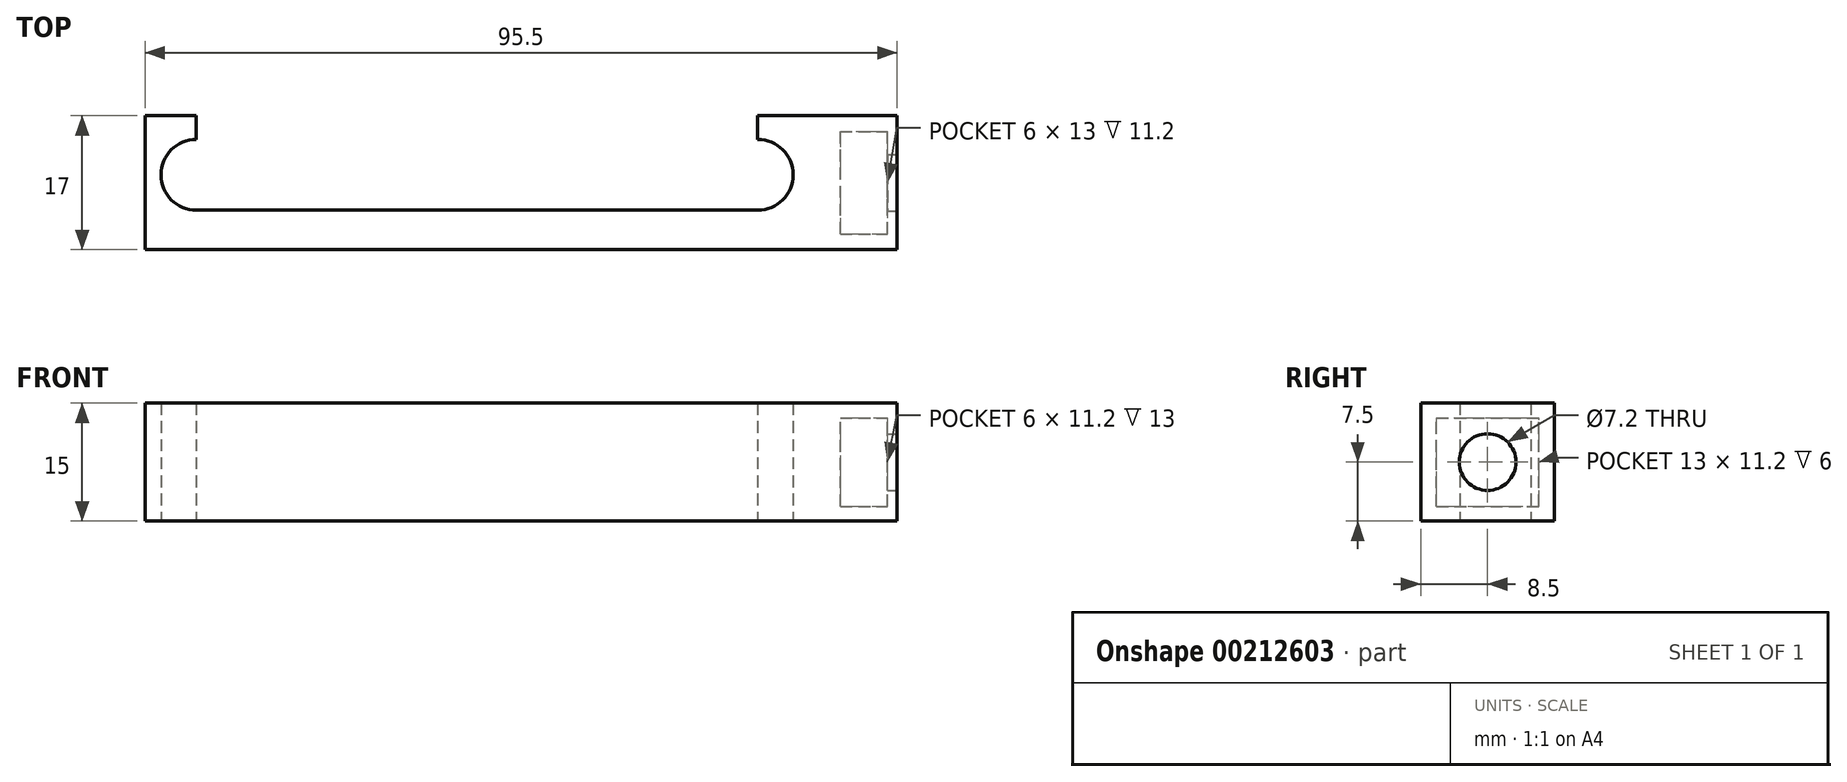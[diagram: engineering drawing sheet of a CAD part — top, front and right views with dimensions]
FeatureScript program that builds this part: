
annotation { "Feature Type Name" : "Feature", "Feature Type Description" : "" }
export const myFeature = defineFeature(function(context is Context, id is Id, definition is map)
    precondition{}
    {
        {
            var Q0;
            Q0=qCreatedBy(makeId("Top.planeOp"),FACE);
            var sketch = newSketch(context, id + "F0", { "sketchPlane" : qUnion([Q0])});
            skLineSegment(sketch, "E0.bottom", {"start": v(35.65, -4.5) * mm, "end": v(-35.65, -4.5) * mm});
            skLineSegment(sketch, "E0.left", {"start": v(40.15, 0) * mm, "end": v(40.15, 0) * mm});
            skLineSegment(sketch, "E0.right", {"start": v(-40.15, 0) * mm, "end": v(-40.15, 0) * mm});
            skPoint(sketch, "E0.middle", {"position": v(0, 0) * mm});
            skPoint(sketch, "E1.visualSharp", {"position": v(-40.15, -4.5) * mm});
            skArc(sketch, "E1.filletArc", {"start": v(-40.15, 0) * mm, "mid": v(-38.83, -3.18) * mm, "end": v(-35.65, -4.5) * mm});
            skPoint(sketch, "E2.visualSharp", {"position": v(-40.15, 4.5) * mm});
            skArc(sketch, "E2.filletArc", {"start": v(-35.65, 4.5) * mm, "mid": v(-38.83, 3.18) * mm, "end": v(-40.15, 0) * mm});
            skPoint(sketch, "E3.visualSharp", {"position": v(40.15, 4.5) * mm});
            skArc(sketch, "E3.filletArc", {"start": v(40.15, 0) * mm, "mid": v(38.83, 3.18) * mm, "end": v(35.65, 4.5) * mm});
            skPoint(sketch, "E4.visualSharp", {"position": v(40.15, -4.5) * mm});
            skArc(sketch, "E4.filletArc", {"start": v(35.65, -4.5) * mm, "mid": v(38.83, -3.18) * mm, "end": v(40.15, 0) * mm});
            skLineSegment(sketch, "E5.bottom", {"start": v(-42.15, 7.5) * mm, "end": v(-35.65, 7.5) * mm});
            skLineSegment(sketch, "E5.top", {"start": v(-42.15, -9.5) * mm, "end": v(52.15, -9.5) * mm});
            skLineSegment(sketch, "E5.left", {"start": v(-42.15, 7.5) * mm, "end": v(-42.15, -9.5) * mm});
            skLineSegment(sketch, "E5.right", {"start": v(52.15, 7.5) * mm, "end": v(52.15, -9.5) * mm});
            skLineSegment(sketch, "E6", {"start": v(-35.65, 4.5) * mm, "end": v(-35.65, 7.5) * mm});
            skLineSegment(sketch, "E7", {"start": v(35.65, 4.5) * mm, "end": v(35.65, 7.5) * mm});
            skLineSegment(sketch, "E8.trimOffspring", {"start": v(35.65, 7.5) * mm, "end": v(52.15, 7.5) * mm});
            skSolve(sketch);
        }
        {
            var Q0;
            Q0=makeQuery(id+"F0.imprint","IMPRINT",FACE,{"disambiguationData":[TD([[makeQuery(id+"F0.imprint","IMPRINT",EDGE,{"derivedFrom":sQuery(id+"F0.wireOp",EDGE,"E0.bottom")}),1.0]])]});
            extrude(context, id + "F1", {"entities" : qUnion([Q0]), "depth" : 15 * mm});
        }
        {
            var Q0;
            Q0=makeQuery(id+"F1.opExtrude","SWEPT_FACE",FACE,{"disambiguationData":[OSD([sQuery(id+"F0.wireOp",EDGE,"E5.right")])]});
            var sketch = newSketch(context, id + "F2", { "sketchPlane" : qUnion([Q0])});
            skLineSegment(sketch, "E9", {"start": v(7.5, 15) * mm, "end": v(-9.5, 0) * mm, "construction": true});
            skLineSegment(sketch, "E10", {"start": v(-9.5, 0) * mm, "end": v(-9.5, 15) * mm, "construction": true});
            skLineSegment(sketch, "E11", {"start": v(-9.5, 15) * mm, "end": v(7.5, 0) * mm, "construction": true});
            skLineSegment(sketch, "E12.bottom", {"start": v(-7.5, 1.9) * mm, "end": v(5.5, 1.9) * mm});
            skLineSegment(sketch, "E12.top", {"start": v(-7.5, 13.1) * mm, "end": v(5.5, 13.1) * mm});
            skLineSegment(sketch, "E12.left", {"start": v(-7.5, 1.9) * mm, "end": v(-7.5, 13.1) * mm});
            skLineSegment(sketch, "E12.right", {"start": v(5.5, 1.9) * mm, "end": v(5.5, 13.1) * mm});
            skPoint(sketch, "E12.middle", {"position": v(-1, 7.5) * mm});
            skSolve(sketch);
        }
        {
            var Q0;
            Q0 = qSketchRegion(id + "F2", true);
            extrude(context, id + "F3", {"entities" : qUnion([Q0]), "operationType" : NewBodyOperationType.REMOVE, "oppositeDirection" : true, "depth" : 6 * mm});
        }
        {
            var Q0;
            Q0=makeQuery(id+"F1.opExtrude","SWEPT_FACE",FACE,{"disambiguationData":[OSD([sQuery(id+"F0.wireOp",EDGE,"E5.right")])]});
            var sketch = newSketch(context, id + "F4", { "sketchPlane" : qUnion([Q0])});
            skLineSegment(sketch, "E13.bottom", {"start": v(7.5, 15) * mm, "end": v(-9.5, 15) * mm});
            skLineSegment(sketch, "E13.top", {"start": v(7.5, 0) * mm, "end": v(-9.5, 0) * mm});
            skLineSegment(sketch, "E13.left", {"start": v(7.5, 15) * mm, "end": v(7.5, 0) * mm});
            skLineSegment(sketch, "E13.right", {"start": v(-9.5, 15) * mm, "end": v(-9.5, 0) * mm});
            skSolve(sketch);
        }
        {
            var Q0;
            Q0 = qSketchRegion(id + "F4", true);
            extrude(context, id + "F5", {"entities" : qUnion([Q0]), "operationType" : NewBodyOperationType.ADD, "depth" : 1.2 * mm});
        }
        {
            var Q0;
            Q0=makeQuery(id+"F5.opExtrude","CAP_FACE",FACE,{"disambiguationData":[OSD([sQuery(id+"F4.wireOp",EDGE,"E13.bottom"),sQuery(id+"F4.wireOp",EDGE,"E13.top"),sQuery(id+"F4.wireOp",EDGE,"E13.left"),sQuery(id+"F4.wireOp",EDGE,"E13.right")])],"isStart":false});
            var sketch = newSketch(context, id + "F6", { "sketchPlane" : qUnion([Q0])});
            skPoint(sketch, "E14.centerSnap0", {"position": v(-9.5, 7.5) * mm});
            skLineSegment(sketch, "E15", {"start": v(7.5, 15) * mm, "end": v(-9.5, 0) * mm, "construction": true});
            skLineSegment(sketch, "E16", {"start": v(-9.5, 0) * mm, "end": v(7.5, 0) * mm, "construction": true});
            skLineSegment(sketch, "E17", {"start": v(7.5, 0) * mm, "end": v(-9.5, 15) * mm, "construction": true});
            skCircle(sketch, "E18", {"center": v(-1, 7.5) * mm, "radius": 3.6 * mm});
            skSolve(sketch);
        }
        {
            var Q0;
            Q0 = qSketchRegion(id + "F6", true);
            extrude(context, id + "F7", {"entities" : qUnion([Q0]), "operationType" : NewBodyOperationType.REMOVE, "oppositeDirection" : true, "depth" : 2 * mm});
        }
    });
